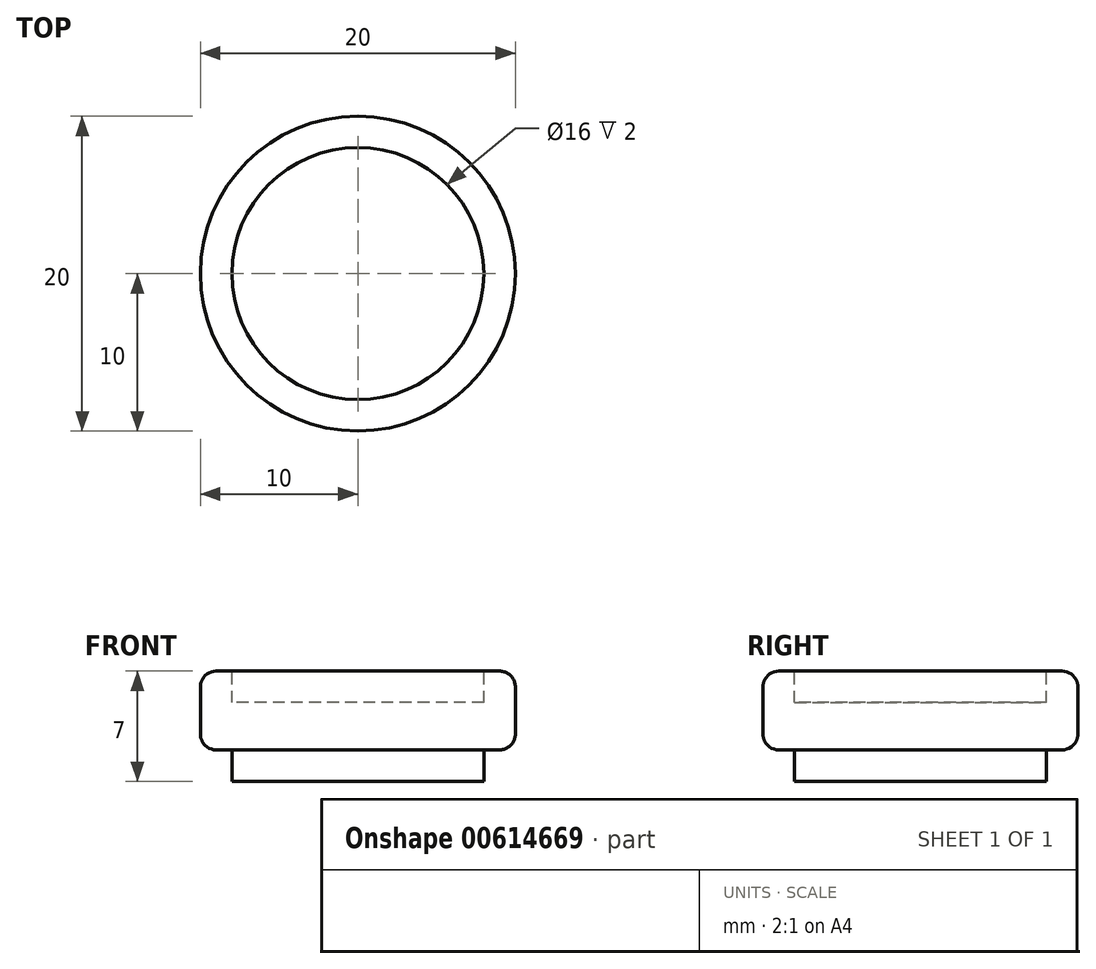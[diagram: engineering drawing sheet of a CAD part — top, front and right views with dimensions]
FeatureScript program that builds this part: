
annotation { "Feature Type Name" : "Feature", "Feature Type Description" : "" }
export const myFeature = defineFeature(function(context is Context, id is Id, definition is map)
    precondition{}
    {
        {
            var Q0;
            Q0=qCreatedBy(makeId("Top.planeOp"),FACE);
            var sketch = newSketch(context, id + "F0", { "sketchPlane" : qUnion([Q0])});
            skCircle(sketch, "E0", {"center": v(0, 0) * mm, "radius": 10 * mm});
            skSolve(sketch);
        }
        {
            var Q0;
            Q0=qSketchRegion(id+"F0",true);
            extrude(context, id + "F1", {"entities" : qUnion([Q0]), "depth" : 5 * mm, "offsetDistance" : 25 * mm});
        }
        {
            var Q0;
            Q0=makeQuery(id+"F1.opExtrude","CAP_FACE",FACE,{"disambiguationData":[OSD([sQuery(id+"F0.wireOp",EDGE,"E0")])],"isStart":true});
            var sketch = newSketch(context, id + "F2", { "sketchPlane" : qUnion([Q0])});
            skCircle(sketch, "E1", {"center": v(0, 0) * mm, "radius": 8 * mm});
            skSolve(sketch);
        }
        {
            var Q0;
            Q0=qSketchRegion(id+"F2",true);
            extrude(context, id + "F3", {"entities" : qUnion([Q0]), "operationType" : NewBodyOperationType.ADD, "depth" : 2 * mm, "offsetDistance" : 25 * mm});
        }
        {
            var Q0;
            Q0=makeQuery(id+"F1.opExtrude","CAP_FACE",FACE,{"disambiguationData":[OSD([sQuery(id+"F0.wireOp",EDGE,"E0")])],"isStart":false});
            var sketch = newSketch(context, id + "F4", { "sketchPlane" : qUnion([Q0])});
            skCircle(sketch, "E2", {"center": v(0, 0) * mm, "radius": 8 * mm});
            skSolve(sketch);
        }
        {
            var Q0;
            Q0 = qSketchRegion(id + "F4", true);
            extrude(context, id + "F5", {"entities" : qUnion([Q0]), "operationType" : NewBodyOperationType.REMOVE, "oppositeDirection" : true, "depth" : 2 * mm, "offsetDistance" : 25 * mm});
        }
        {
            var Q0;
            Q0=makeQuery(id+"F3.opExtrude","CAP_EDGE",EDGE,{"disambiguationData":[OSD([sQuery(id+"F2.wireOp",EDGE,"E1")])],"isStart":true});
            var Q1;
            Q1=makeQuery(id+"F1.opExtrude","CAP_EDGE",EDGE,{"disambiguationData":[OSD([sQuery(id+"F0.wireOp",EDGE,"E0")])],"isStart":true});
            var Q2;
            Q2=makeQuery(id+"F1.opExtrude","CAP_EDGE",EDGE,{"disambiguationData":[OSD([sQuery(id+"F0.wireOp",EDGE,"E0")])],"isStart":false});
            var Q3;
            Q3=makeQuery(id+"F5.boolean.opBoolean","COPY",EDGE,{"derivedFrom":makeQuery(id+"F5.opExtrude","CAP_EDGE",EDGE,{"disambiguationData":[OSD([sQuery(id+"F4.wireOp",EDGE,"E2")])],"isStart":true})});
            fillet(context, id + "F6", {"entities" : qUnion([Q0, Q1, Q2, Q3]), "radius" : 1 * mm, "tangentPropagation" : true, "allowEdgeOverflow" : false});
        }
    });
